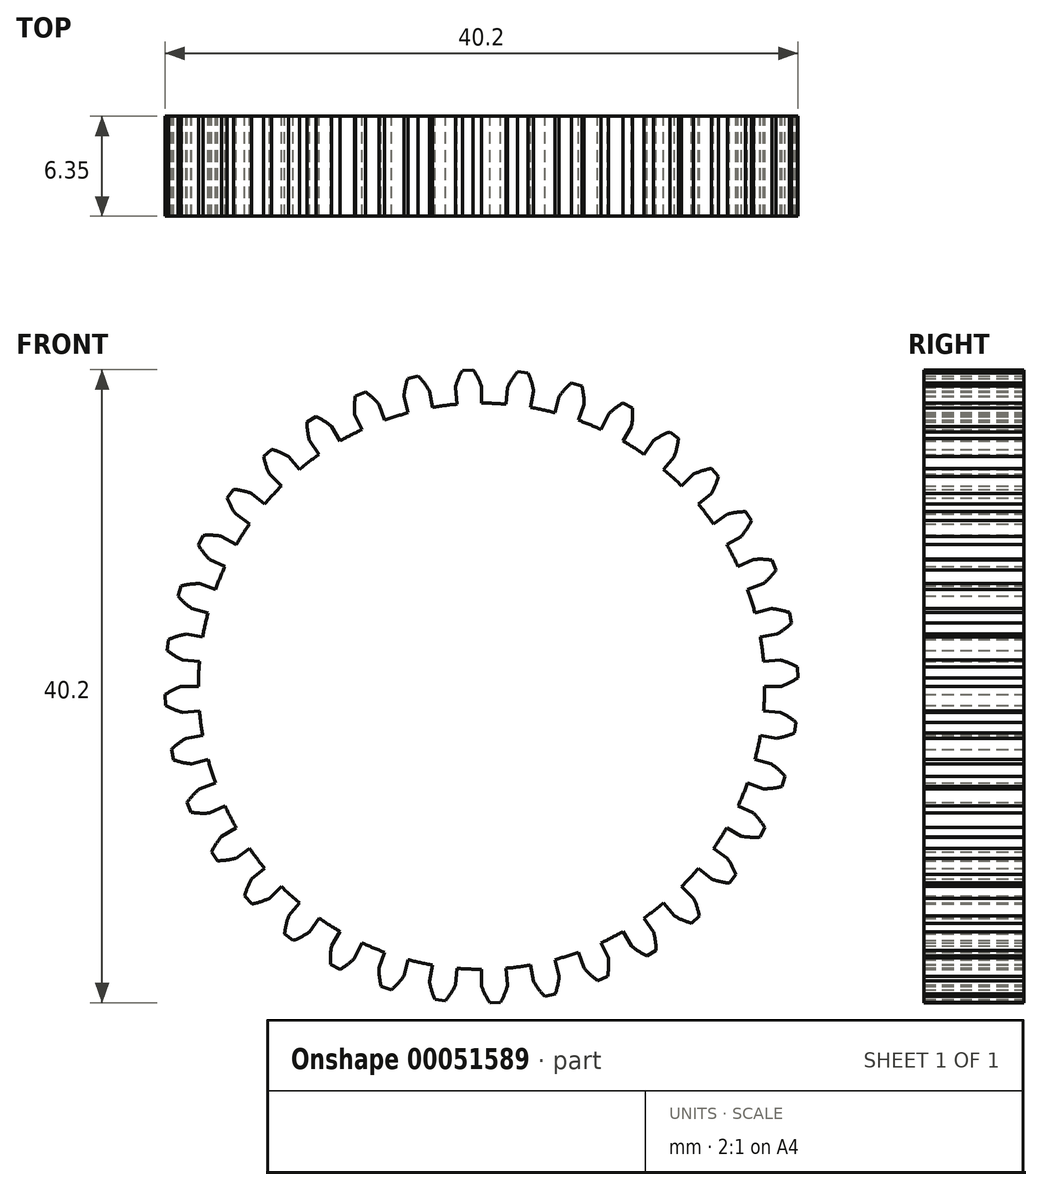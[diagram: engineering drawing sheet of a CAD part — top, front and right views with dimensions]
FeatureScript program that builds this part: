
annotation { "Feature Type Name" : "Feature", "Feature Type Description" : "" }
export const myFeature = defineFeature(function(context is Context, id is Id, definition is map)
    precondition{}
    {
        {
            var Q0;
            Q0=qCreatedBy(makeId("Front.planeOp"),FACE);
            var sketch = newSketch(context, id + "F0", { "sketchPlane" : qUnion([Q0])});
            skArc(sketch, "E0", {"start": v(-1.38, 17.93) * mm, "mid": v(-2.35, 17.83) * mm, "end": v(-3.3, 17.68) * mm});
            skArc(sketch, "E1.trimOffspring", {"start": v(0, 19.05) * mm, "mid": v(-0.24, 19.6) * mm, "end": v(-0.54, 20.1) * mm});
            skLineSegment(sketch, "E2", {"start": v(0, 19.05) * mm, "end": v(0, 17.98) * mm});
            skLineSegment(sketch, "E3", {"start": v(-0.54, 20.1) * mm, "end": v(-0.88, 20.08) * mm});
            skArc(sketch, "E4.MirrorCS", {"start": v(-1.66, 18.98) * mm, "mid": v(-1.47, 19.54) * mm, "end": v(-1.22, 20.07) * mm});
            skLineSegment(sketch, "E5.MirrorCS", {"start": v(-1.22, 20.07) * mm, "end": v(-0.88, 20.08) * mm});
            skLineSegment(sketch, "E6.MirrorCS", {"start": v(-1.66, 18.98) * mm, "end": v(-1.57, 17.91) * mm});
            skLineSegment(sketch, "E7.1.0", {"start": v(-4.93, 18.4) * mm, "end": v(-4.65, 17.37) * mm});
            skArc(sketch, "E7.1.1", {"start": v(-4.93, 18.4) * mm, "mid": v(-4.84, 18.98) * mm, "end": v(-4.68, 19.55) * mm});
            skLineSegment(sketch, "E7.1.2", {"start": v(-4.68, 19.55) * mm, "end": v(-4.35, 19.62) * mm});
            skLineSegment(sketch, "E7.1.3", {"start": v(-4.02, 19.7) * mm, "end": v(-4.35, 19.62) * mm});
            skArc(sketch, "E7.1.4", {"start": v(-3.3, 18.76) * mm, "mid": v(-3.63, 19.25) * mm, "end": v(-4.02, 19.7) * mm});
            skLineSegment(sketch, "E7.1.5", {"start": v(-3.3, 18.76) * mm, "end": v(-3.12, 17.7) * mm});
            skLineSegment(sketch, "E7.2.0", {"start": v(-8.05, 17.27) * mm, "end": v(-7.6, 16.3) * mm});
            skArc(sketch, "E7.2.1", {"start": v(-8.05, 17.27) * mm, "mid": v(-8.07, 17.85) * mm, "end": v(-8, 18.44) * mm});
            skLineSegment(sketch, "E7.2.2", {"start": v(-8, 18.44) * mm, "end": v(-7.7, 18.57) * mm});
            skLineSegment(sketch, "E7.2.3", {"start": v(-7.38, 18.7) * mm, "end": v(-7.7, 18.57) * mm});
            skArc(sketch, "E7.2.4", {"start": v(-6.52, 17.9) * mm, "mid": v(-6.92, 18.33) * mm, "end": v(-7.38, 18.7) * mm});
            skLineSegment(sketch, "E7.2.5", {"start": v(-6.52, 17.9) * mm, "end": v(-6.15, 16.9) * mm});
            skLineSegment(sketch, "E7.3.0", {"start": v(-10.93, 15.6) * mm, "end": v(-10.31, 14.73) * mm});
            skArc(sketch, "E7.3.1", {"start": v(-10.93, 15.6) * mm, "mid": v(-11.04, 16.18) * mm, "end": v(-11.09, 16.77) * mm});
            skLineSegment(sketch, "E7.3.2", {"start": v(-11.09, 16.77) * mm, "end": v(-10.8, 16.95) * mm});
            skLineSegment(sketch, "E7.3.3", {"start": v(-10.51, 17.14) * mm, "end": v(-10.8, 16.95) * mm});
            skArc(sketch, "E7.3.4", {"start": v(-9.52, 16.5) * mm, "mid": v(-10, 16.85) * mm, "end": v(-10.51, 17.14) * mm});
            skLineSegment(sketch, "E7.3.5", {"start": v(-9.52, 16.5) * mm, "end": v(-9, 15.57) * mm});
            skLineSegment(sketch, "E7.4.0", {"start": v(-13.47, 13.47) * mm, "end": v(-12.72, 12.72) * mm});
            skArc(sketch, "E7.4.1", {"start": v(-13.47, 13.47) * mm, "mid": v(-13.69, 14.02) * mm, "end": v(-13.83, 14.6) * mm});
            skLineSegment(sketch, "E7.4.2", {"start": v(-13.83, 14.6) * mm, "end": v(-13.58, 14.82) * mm});
            skLineSegment(sketch, "E7.4.3", {"start": v(-13.33, 15.05) * mm, "end": v(-13.58, 14.82) * mm});
            skArc(sketch, "E7.4.4", {"start": v(-12.25, 14.6) * mm, "mid": v(-12.77, 14.86) * mm, "end": v(-13.33, 15.05) * mm});
            skLineSegment(sketch, "E7.4.5", {"start": v(-12.25, 14.6) * mm, "end": v(-11.56, 13.78) * mm});
            skLineSegment(sketch, "E7.5.0", {"start": v(-15.6, 10.93) * mm, "end": v(-14.73, 10.31) * mm});
            skArc(sketch, "E7.5.1", {"start": v(-15.6, 10.93) * mm, "mid": v(-15.91, 11.43) * mm, "end": v(-16.15, 11.97) * mm});
            skLineSegment(sketch, "E7.5.2", {"start": v(-16.15, 11.97) * mm, "end": v(-15.95, 12.24) * mm});
            skLineSegment(sketch, "E7.5.3", {"start": v(-15.74, 12.5) * mm, "end": v(-15.95, 12.24) * mm});
            skArc(sketch, "E7.5.4", {"start": v(-14.6, 12.25) * mm, "mid": v(-15.16, 12.41) * mm, "end": v(-15.74, 12.5) * mm});
            skLineSegment(sketch, "E7.5.5", {"start": v(-14.6, 12.25) * mm, "end": v(-13.78, 11.56) * mm});
            skLineSegment(sketch, "E7.6.0", {"start": v(-17.27, 8.05) * mm, "end": v(-16.3, 7.6) * mm});
            skArc(sketch, "E7.6.1", {"start": v(-17.27, 8.05) * mm, "mid": v(-17.65, 8.5) * mm, "end": v(-17.99, 8.98) * mm});
            skLineSegment(sketch, "E7.6.2", {"start": v(-17.99, 8.98) * mm, "end": v(-17.83, 9.28) * mm});
            skLineSegment(sketch, "E7.6.3", {"start": v(-17.67, 9.58) * mm, "end": v(-17.83, 9.28) * mm});
            skArc(sketch, "E7.6.4", {"start": v(-16.5, 9.53) * mm, "mid": v(-17.08, 9.6) * mm, "end": v(-17.67, 9.58) * mm});
            skLineSegment(sketch, "E7.6.5", {"start": v(-16.5, 9.53) * mm, "end": v(-15.57, 9) * mm});
            skLineSegment(sketch, "E7.7.0", {"start": v(-18.4, 4.93) * mm, "end": v(-17.37, 4.65) * mm});
            skArc(sketch, "E7.7.1", {"start": v(-18.4, 4.93) * mm, "mid": v(-18.86, 5.3) * mm, "end": v(-19.27, 5.72) * mm});
            skLineSegment(sketch, "E7.7.2", {"start": v(-19.27, 5.72) * mm, "end": v(-19.17, 6.04) * mm});
            skLineSegment(sketch, "E7.7.3", {"start": v(-19.07, 6.37) * mm, "end": v(-19.17, 6.04) * mm});
            skArc(sketch, "E7.7.4", {"start": v(-17.9, 6.52) * mm, "mid": v(-18.49, 6.48) * mm, "end": v(-19.07, 6.37) * mm});
            skLineSegment(sketch, "E7.7.5", {"start": v(-17.9, 6.52) * mm, "end": v(-16.9, 6.15) * mm});
            skLineSegment(sketch, "E7.8.0", {"start": v(-18.98, 1.66) * mm, "end": v(-17.91, 1.57) * mm});
            skArc(sketch, "E7.8.1", {"start": v(-18.98, 1.66) * mm, "mid": v(-19.5, 1.94) * mm, "end": v(-19.97, 2.29) * mm});
            skLineSegment(sketch, "E7.8.2", {"start": v(-19.97, 2.29) * mm, "end": v(-19.93, 2.62) * mm});
            skLineSegment(sketch, "E7.8.3", {"start": v(-19.88, 2.96) * mm, "end": v(-19.93, 2.62) * mm});
            skArc(sketch, "E7.8.4", {"start": v(-18.76, 3.3) * mm, "mid": v(-19.33, 3.17) * mm, "end": v(-19.88, 2.96) * mm});
            skLineSegment(sketch, "E7.8.5", {"start": v(-18.76, 3.3) * mm, "end": v(-17.7, 3.12) * mm});
            skLineSegment(sketch, "E7.9.0", {"start": v(-18.98, -1.66) * mm, "end": v(-17.91, -1.57) * mm});
            skArc(sketch, "E7.9.1", {"start": v(-18.98, -1.66) * mm, "mid": v(-19.54, -1.47) * mm, "end": v(-20.07, -1.22) * mm});
            skLineSegment(sketch, "E7.9.2", {"start": v(-20.07, -1.22) * mm, "end": v(-20.08, -0.88) * mm});
            skLineSegment(sketch, "E7.9.3", {"start": v(-20.1, -0.54) * mm, "end": v(-20.08, -0.88) * mm});
            skArc(sketch, "E7.9.4", {"start": v(-19.05, 0) * mm, "mid": v(-19.6, -0.24) * mm, "end": v(-20.1, -0.54) * mm});
            skLineSegment(sketch, "E7.9.5", {"start": v(-19.05, 0) * mm, "end": v(-17.98, 0) * mm});
            skLineSegment(sketch, "E7.10.0", {"start": v(-18.4, -4.93) * mm, "end": v(-17.37, -4.65) * mm});
            skArc(sketch, "E7.10.1", {"start": v(-18.4, -4.93) * mm, "mid": v(-18.98, -4.84) * mm, "end": v(-19.55, -4.68) * mm});
            skLineSegment(sketch, "E7.10.2", {"start": v(-19.55, -4.68) * mm, "end": v(-19.62, -4.35) * mm});
            skLineSegment(sketch, "E7.10.3", {"start": v(-19.7, -4.02) * mm, "end": v(-19.62, -4.35) * mm});
            skArc(sketch, "E7.10.4", {"start": v(-18.76, -3.3) * mm, "mid": v(-19.25, -3.63) * mm, "end": v(-19.7, -4.02) * mm});
            skLineSegment(sketch, "E7.10.5", {"start": v(-18.76, -3.3) * mm, "end": v(-17.7, -3.12) * mm});
            skLineSegment(sketch, "E7.11.0", {"start": v(-17.27, -8.05) * mm, "end": v(-16.3, -7.6) * mm});
            skArc(sketch, "E7.11.1", {"start": v(-17.27, -8.05) * mm, "mid": v(-17.85, -8.07) * mm, "end": v(-18.44, -8) * mm});
            skLineSegment(sketch, "E7.11.2", {"start": v(-18.44, -8) * mm, "end": v(-18.57, -7.7) * mm});
            skLineSegment(sketch, "E7.11.3", {"start": v(-18.7, -7.38) * mm, "end": v(-18.57, -7.7) * mm});
            skArc(sketch, "E7.11.4", {"start": v(-17.9, -6.52) * mm, "mid": v(-18.33, -6.92) * mm, "end": v(-18.7, -7.38) * mm});
            skLineSegment(sketch, "E7.11.5", {"start": v(-17.9, -6.52) * mm, "end": v(-16.9, -6.15) * mm});
            skLineSegment(sketch, "E7.12.0", {"start": v(-15.6, -10.93) * mm, "end": v(-14.73, -10.31) * mm});
            skArc(sketch, "E7.12.1", {"start": v(-15.6, -10.93) * mm, "mid": v(-16.18, -11.04) * mm, "end": v(-16.77, -11.09) * mm});
            skLineSegment(sketch, "E7.12.2", {"start": v(-16.77, -11.09) * mm, "end": v(-16.95, -10.8) * mm});
            skLineSegment(sketch, "E7.12.3", {"start": v(-17.14, -10.51) * mm, "end": v(-16.95, -10.8) * mm});
            skArc(sketch, "E7.12.4", {"start": v(-16.5, -9.52) * mm, "mid": v(-16.85, -10) * mm, "end": v(-17.14, -10.51) * mm});
            skLineSegment(sketch, "E7.12.5", {"start": v(-16.5, -9.52) * mm, "end": v(-15.57, -9) * mm});
            skLineSegment(sketch, "E7.13.0", {"start": v(-13.47, -13.47) * mm, "end": v(-12.72, -12.72) * mm});
            skArc(sketch, "E7.13.1", {"start": v(-13.47, -13.47) * mm, "mid": v(-14.02, -13.69) * mm, "end": v(-14.6, -13.83) * mm});
            skLineSegment(sketch, "E7.13.2", {"start": v(-14.6, -13.83) * mm, "end": v(-14.82, -13.58) * mm});
            skLineSegment(sketch, "E7.13.3", {"start": v(-15.05, -13.33) * mm, "end": v(-14.82, -13.58) * mm});
            skArc(sketch, "E7.13.4", {"start": v(-14.6, -12.25) * mm, "mid": v(-14.86, -12.77) * mm, "end": v(-15.05, -13.33) * mm});
            skLineSegment(sketch, "E7.13.5", {"start": v(-14.6, -12.25) * mm, "end": v(-13.78, -11.56) * mm});
            skLineSegment(sketch, "E7.14.0", {"start": v(-10.93, -15.6) * mm, "end": v(-10.31, -14.73) * mm});
            skArc(sketch, "E7.14.1", {"start": v(-10.93, -15.6) * mm, "mid": v(-11.43, -15.91) * mm, "end": v(-11.97, -16.15) * mm});
            skLineSegment(sketch, "E7.14.2", {"start": v(-11.97, -16.15) * mm, "end": v(-12.24, -15.95) * mm});
            skLineSegment(sketch, "E7.14.3", {"start": v(-12.5, -15.74) * mm, "end": v(-12.24, -15.95) * mm});
            skArc(sketch, "E7.14.4", {"start": v(-12.25, -14.6) * mm, "mid": v(-12.41, -15.16) * mm, "end": v(-12.5, -15.74) * mm});
            skLineSegment(sketch, "E7.14.5", {"start": v(-12.25, -14.6) * mm, "end": v(-11.56, -13.78) * mm});
            skLineSegment(sketch, "E7.15.0", {"start": v(-8.05, -17.27) * mm, "end": v(-7.6, -16.3) * mm});
            skArc(sketch, "E7.15.1", {"start": v(-8.05, -17.27) * mm, "mid": v(-8.5, -17.65) * mm, "end": v(-8.98, -17.99) * mm});
            skLineSegment(sketch, "E7.15.2", {"start": v(-8.98, -17.99) * mm, "end": v(-9.28, -17.83) * mm});
            skLineSegment(sketch, "E7.15.3", {"start": v(-9.58, -17.67) * mm, "end": v(-9.28, -17.83) * mm});
            skArc(sketch, "E7.15.4", {"start": v(-9.53, -16.5) * mm, "mid": v(-9.6, -17.08) * mm, "end": v(-9.58, -17.67) * mm});
            skLineSegment(sketch, "E7.15.5", {"start": v(-9.53, -16.5) * mm, "end": v(-9, -15.57) * mm});
            skLineSegment(sketch, "E7.16.0", {"start": v(-4.93, -18.4) * mm, "end": v(-4.65, -17.37) * mm});
            skArc(sketch, "E7.16.1", {"start": v(-4.93, -18.4) * mm, "mid": v(-5.3, -18.86) * mm, "end": v(-5.72, -19.27) * mm});
            skLineSegment(sketch, "E7.16.2", {"start": v(-5.72, -19.27) * mm, "end": v(-6.04, -19.17) * mm});
            skLineSegment(sketch, "E7.16.3", {"start": v(-6.37, -19.07) * mm, "end": v(-6.04, -19.17) * mm});
            skArc(sketch, "E7.16.4", {"start": v(-6.52, -17.9) * mm, "mid": v(-6.48, -18.49) * mm, "end": v(-6.37, -19.07) * mm});
            skLineSegment(sketch, "E7.16.5", {"start": v(-6.52, -17.9) * mm, "end": v(-6.15, -16.9) * mm});
            skLineSegment(sketch, "E7.17.0", {"start": v(-1.66, -18.98) * mm, "end": v(-1.57, -17.91) * mm});
            skArc(sketch, "E7.17.1", {"start": v(-1.66, -18.98) * mm, "mid": v(-1.94, -19.5) * mm, "end": v(-2.29, -19.97) * mm});
            skLineSegment(sketch, "E7.17.2", {"start": v(-2.29, -19.97) * mm, "end": v(-2.62, -19.93) * mm});
            skLineSegment(sketch, "E7.17.3", {"start": v(-2.96, -19.88) * mm, "end": v(-2.62, -19.93) * mm});
            skArc(sketch, "E7.17.4", {"start": v(-3.3, -18.76) * mm, "mid": v(-3.17, -19.33) * mm, "end": v(-2.96, -19.88) * mm});
            skLineSegment(sketch, "E7.17.5", {"start": v(-3.3, -18.76) * mm, "end": v(-3.12, -17.7) * mm});
            skLineSegment(sketch, "E7.18.0", {"start": v(1.66, -18.98) * mm, "end": v(1.57, -17.91) * mm});
            skArc(sketch, "E7.18.1", {"start": v(1.66, -18.98) * mm, "mid": v(1.47, -19.54) * mm, "end": v(1.22, -20.07) * mm});
            skLineSegment(sketch, "E7.18.2", {"start": v(1.22, -20.07) * mm, "end": v(0.88, -20.08) * mm});
            skLineSegment(sketch, "E7.18.3", {"start": v(0.54, -20.1) * mm, "end": v(0.88, -20.08) * mm});
            skArc(sketch, "E7.18.4", {"start": v(0, -19.05) * mm, "mid": v(0.24, -19.6) * mm, "end": v(0.54, -20.1) * mm});
            skLineSegment(sketch, "E7.18.5", {"start": v(0, -19.05) * mm, "end": v(0, -17.98) * mm});
            skLineSegment(sketch, "E7.19.0", {"start": v(4.93, -18.4) * mm, "end": v(4.65, -17.37) * mm});
            skArc(sketch, "E7.19.1", {"start": v(4.93, -18.4) * mm, "mid": v(4.84, -18.98) * mm, "end": v(4.68, -19.55) * mm});
            skLineSegment(sketch, "E7.19.2", {"start": v(4.68, -19.55) * mm, "end": v(4.35, -19.62) * mm});
            skLineSegment(sketch, "E7.19.3", {"start": v(4.02, -19.7) * mm, "end": v(4.35, -19.62) * mm});
            skArc(sketch, "E7.19.4", {"start": v(3.3, -18.76) * mm, "mid": v(3.63, -19.25) * mm, "end": v(4.02, -19.7) * mm});
            skLineSegment(sketch, "E7.19.5", {"start": v(3.3, -18.76) * mm, "end": v(3.12, -17.7) * mm});
            skLineSegment(sketch, "E7.20.0", {"start": v(8.05, -17.27) * mm, "end": v(7.6, -16.3) * mm});
            skArc(sketch, "E7.20.1", {"start": v(8.05, -17.27) * mm, "mid": v(8.07, -17.85) * mm, "end": v(8, -18.44) * mm});
            skLineSegment(sketch, "E7.20.2", {"start": v(8, -18.44) * mm, "end": v(7.7, -18.57) * mm});
            skLineSegment(sketch, "E7.20.3", {"start": v(7.38, -18.7) * mm, "end": v(7.7, -18.57) * mm});
            skArc(sketch, "E7.20.4", {"start": v(6.52, -17.9) * mm, "mid": v(6.92, -18.33) * mm, "end": v(7.38, -18.7) * mm});
            skLineSegment(sketch, "E7.20.5", {"start": v(6.52, -17.9) * mm, "end": v(6.15, -16.9) * mm});
            skLineSegment(sketch, "E7.21.0", {"start": v(10.93, -15.6) * mm, "end": v(10.31, -14.73) * mm});
            skArc(sketch, "E7.21.1", {"start": v(10.93, -15.6) * mm, "mid": v(11.04, -16.18) * mm, "end": v(11.09, -16.77) * mm});
            skLineSegment(sketch, "E7.21.2", {"start": v(11.09, -16.77) * mm, "end": v(10.8, -16.95) * mm});
            skLineSegment(sketch, "E7.21.3", {"start": v(10.51, -17.14) * mm, "end": v(10.8, -16.95) * mm});
            skArc(sketch, "E7.21.4", {"start": v(9.53, -16.5) * mm, "mid": v(10, -16.85) * mm, "end": v(10.51, -17.14) * mm});
            skLineSegment(sketch, "E7.21.5", {"start": v(9.53, -16.5) * mm, "end": v(9, -15.57) * mm});
            skLineSegment(sketch, "E7.22.0", {"start": v(13.47, -13.47) * mm, "end": v(12.72, -12.72) * mm});
            skArc(sketch, "E7.22.1", {"start": v(13.47, -13.47) * mm, "mid": v(13.69, -14.02) * mm, "end": v(13.83, -14.6) * mm});
            skLineSegment(sketch, "E7.22.2", {"start": v(13.83, -14.6) * mm, "end": v(13.58, -14.82) * mm});
            skLineSegment(sketch, "E7.22.3", {"start": v(13.33, -15.05) * mm, "end": v(13.58, -14.82) * mm});
            skArc(sketch, "E7.22.4", {"start": v(12.25, -14.6) * mm, "mid": v(12.77, -14.86) * mm, "end": v(13.33, -15.05) * mm});
            skLineSegment(sketch, "E7.22.5", {"start": v(12.25, -14.6) * mm, "end": v(11.56, -13.78) * mm});
            skLineSegment(sketch, "E7.23.0", {"start": v(15.6, -10.93) * mm, "end": v(14.73, -10.31) * mm});
            skArc(sketch, "E7.23.1", {"start": v(15.6, -10.93) * mm, "mid": v(15.91, -11.43) * mm, "end": v(16.15, -11.97) * mm});
            skLineSegment(sketch, "E7.23.2", {"start": v(16.15, -11.97) * mm, "end": v(15.95, -12.24) * mm});
            skLineSegment(sketch, "E7.23.3", {"start": v(15.74, -12.5) * mm, "end": v(15.95, -12.24) * mm});
            skArc(sketch, "E7.23.4", {"start": v(14.6, -12.25) * mm, "mid": v(15.16, -12.41) * mm, "end": v(15.74, -12.5) * mm});
            skLineSegment(sketch, "E7.23.5", {"start": v(14.6, -12.25) * mm, "end": v(13.78, -11.56) * mm});
            skLineSegment(sketch, "E7.24.0", {"start": v(17.27, -8.05) * mm, "end": v(16.3, -7.6) * mm});
            skArc(sketch, "E7.24.1", {"start": v(17.27, -8.05) * mm, "mid": v(17.65, -8.5) * mm, "end": v(17.99, -8.98) * mm});
            skLineSegment(sketch, "E7.24.2", {"start": v(17.99, -8.98) * mm, "end": v(17.83, -9.28) * mm});
            skLineSegment(sketch, "E7.24.3", {"start": v(17.67, -9.58) * mm, "end": v(17.83, -9.28) * mm});
            skArc(sketch, "E7.24.4", {"start": v(16.5, -9.53) * mm, "mid": v(17.08, -9.6) * mm, "end": v(17.67, -9.58) * mm});
            skLineSegment(sketch, "E7.24.5", {"start": v(16.5, -9.53) * mm, "end": v(15.57, -9) * mm});
            skLineSegment(sketch, "E7.25.0", {"start": v(18.4, -4.93) * mm, "end": v(17.37, -4.65) * mm});
            skArc(sketch, "E7.25.1", {"start": v(18.4, -4.93) * mm, "mid": v(18.86, -5.3) * mm, "end": v(19.27, -5.72) * mm});
            skLineSegment(sketch, "E7.25.2", {"start": v(19.27, -5.72) * mm, "end": v(19.17, -6.04) * mm});
            skLineSegment(sketch, "E7.25.3", {"start": v(19.07, -6.37) * mm, "end": v(19.17, -6.04) * mm});
            skArc(sketch, "E7.25.4", {"start": v(17.9, -6.52) * mm, "mid": v(18.49, -6.48) * mm, "end": v(19.07, -6.37) * mm});
            skLineSegment(sketch, "E7.25.5", {"start": v(17.9, -6.52) * mm, "end": v(16.9, -6.15) * mm});
            skLineSegment(sketch, "E7.26.0", {"start": v(18.98, -1.66) * mm, "end": v(17.91, -1.57) * mm});
            skArc(sketch, "E7.26.1", {"start": v(18.98, -1.66) * mm, "mid": v(19.5, -1.94) * mm, "end": v(19.97, -2.29) * mm});
            skLineSegment(sketch, "E7.26.2", {"start": v(19.97, -2.29) * mm, "end": v(19.93, -2.62) * mm});
            skLineSegment(sketch, "E7.26.3", {"start": v(19.88, -2.96) * mm, "end": v(19.93, -2.62) * mm});
            skArc(sketch, "E7.26.4", {"start": v(18.76, -3.3) * mm, "mid": v(19.33, -3.17) * mm, "end": v(19.88, -2.96) * mm});
            skLineSegment(sketch, "E7.26.5", {"start": v(18.76, -3.3) * mm, "end": v(17.7, -3.12) * mm});
            skLineSegment(sketch, "E7.27.0", {"start": v(18.98, 1.66) * mm, "end": v(17.91, 1.57) * mm});
            skArc(sketch, "E7.27.1", {"start": v(18.98, 1.66) * mm, "mid": v(19.54, 1.47) * mm, "end": v(20.07, 1.22) * mm});
            skLineSegment(sketch, "E7.27.2", {"start": v(20.07, 1.22) * mm, "end": v(20.08, 0.88) * mm});
            skLineSegment(sketch, "E7.27.3", {"start": v(20.1, 0.54) * mm, "end": v(20.08, 0.88) * mm});
            skArc(sketch, "E7.27.4", {"start": v(19.05, 0) * mm, "mid": v(19.6, 0.24) * mm, "end": v(20.1, 0.54) * mm});
            skLineSegment(sketch, "E7.27.5", {"start": v(19.05, 0) * mm, "end": v(17.98, 0) * mm});
            skLineSegment(sketch, "E7.28.0", {"start": v(18.4, 4.93) * mm, "end": v(17.37, 4.65) * mm});
            skArc(sketch, "E7.28.1", {"start": v(18.4, 4.93) * mm, "mid": v(18.98, 4.84) * mm, "end": v(19.55, 4.68) * mm});
            skLineSegment(sketch, "E7.28.2", {"start": v(19.55, 4.68) * mm, "end": v(19.62, 4.35) * mm});
            skLineSegment(sketch, "E7.28.3", {"start": v(19.7, 4.02) * mm, "end": v(19.62, 4.35) * mm});
            skArc(sketch, "E7.28.4", {"start": v(18.76, 3.3) * mm, "mid": v(19.25, 3.63) * mm, "end": v(19.7, 4.02) * mm});
            skLineSegment(sketch, "E7.28.5", {"start": v(18.76, 3.3) * mm, "end": v(17.7, 3.12) * mm});
            skLineSegment(sketch, "E7.29.0", {"start": v(17.27, 8.05) * mm, "end": v(16.3, 7.6) * mm});
            skArc(sketch, "E7.29.1", {"start": v(17.27, 8.05) * mm, "mid": v(17.85, 8.07) * mm, "end": v(18.44, 8) * mm});
            skLineSegment(sketch, "E7.29.2", {"start": v(18.44, 8) * mm, "end": v(18.57, 7.7) * mm});
            skLineSegment(sketch, "E7.29.3", {"start": v(18.7, 7.38) * mm, "end": v(18.57, 7.7) * mm});
            skArc(sketch, "E7.29.4", {"start": v(17.9, 6.52) * mm, "mid": v(18.33, 6.92) * mm, "end": v(18.7, 7.38) * mm});
            skLineSegment(sketch, "E7.29.5", {"start": v(17.9, 6.52) * mm, "end": v(16.9, 6.15) * mm});
            skLineSegment(sketch, "E7.30.0", {"start": v(15.6, 10.93) * mm, "end": v(14.73, 10.31) * mm});
            skArc(sketch, "E7.30.1", {"start": v(15.6, 10.93) * mm, "mid": v(16.18, 11.04) * mm, "end": v(16.77, 11.09) * mm});
            skLineSegment(sketch, "E7.30.2", {"start": v(16.77, 11.09) * mm, "end": v(16.95, 10.8) * mm});
            skLineSegment(sketch, "E7.30.3", {"start": v(17.14, 10.51) * mm, "end": v(16.95, 10.8) * mm});
            skArc(sketch, "E7.30.4", {"start": v(16.5, 9.52) * mm, "mid": v(16.85, 10) * mm, "end": v(17.14, 10.51) * mm});
            skLineSegment(sketch, "E7.30.5", {"start": v(16.5, 9.52) * mm, "end": v(15.57, 9) * mm});
            skLineSegment(sketch, "E7.31.0", {"start": v(13.47, 13.47) * mm, "end": v(12.72, 12.72) * mm});
            skArc(sketch, "E7.31.1", {"start": v(13.47, 13.47) * mm, "mid": v(14.02, 13.69) * mm, "end": v(14.6, 13.83) * mm});
            skLineSegment(sketch, "E7.31.2", {"start": v(14.6, 13.83) * mm, "end": v(14.82, 13.58) * mm});
            skLineSegment(sketch, "E7.31.3", {"start": v(15.05, 13.33) * mm, "end": v(14.82, 13.58) * mm});
            skArc(sketch, "E7.31.4", {"start": v(14.6, 12.25) * mm, "mid": v(14.86, 12.77) * mm, "end": v(15.05, 13.33) * mm});
            skLineSegment(sketch, "E7.31.5", {"start": v(14.6, 12.25) * mm, "end": v(13.78, 11.56) * mm});
            skLineSegment(sketch, "E7.32.0", {"start": v(10.93, 15.6) * mm, "end": v(10.31, 14.73) * mm});
            skArc(sketch, "E7.32.1", {"start": v(10.93, 15.6) * mm, "mid": v(11.43, 15.91) * mm, "end": v(11.97, 16.15) * mm});
            skLineSegment(sketch, "E7.32.2", {"start": v(11.97, 16.15) * mm, "end": v(12.24, 15.95) * mm});
            skLineSegment(sketch, "E7.32.3", {"start": v(12.5, 15.74) * mm, "end": v(12.24, 15.95) * mm});
            skArc(sketch, "E7.32.4", {"start": v(12.25, 14.6) * mm, "mid": v(12.41, 15.16) * mm, "end": v(12.5, 15.74) * mm});
            skLineSegment(sketch, "E7.32.5", {"start": v(12.25, 14.6) * mm, "end": v(11.56, 13.78) * mm});
            skLineSegment(sketch, "E7.33.0", {"start": v(8.05, 17.27) * mm, "end": v(7.6, 16.3) * mm});
            skArc(sketch, "E7.33.1", {"start": v(8.05, 17.27) * mm, "mid": v(8.5, 17.65) * mm, "end": v(8.98, 17.99) * mm});
            skLineSegment(sketch, "E7.33.2", {"start": v(8.98, 17.99) * mm, "end": v(9.28, 17.83) * mm});
            skLineSegment(sketch, "E7.33.3", {"start": v(9.58, 17.67) * mm, "end": v(9.28, 17.83) * mm});
            skArc(sketch, "E7.33.4", {"start": v(9.52, 16.5) * mm, "mid": v(9.6, 17.08) * mm, "end": v(9.58, 17.67) * mm});
            skLineSegment(sketch, "E7.33.5", {"start": v(9.52, 16.5) * mm, "end": v(9, 15.57) * mm});
            skLineSegment(sketch, "E7.34.0", {"start": v(4.93, 18.4) * mm, "end": v(4.65, 17.37) * mm});
            skArc(sketch, "E7.34.1", {"start": v(4.93, 18.4) * mm, "mid": v(5.3, 18.86) * mm, "end": v(5.72, 19.27) * mm});
            skLineSegment(sketch, "E7.34.2", {"start": v(5.72, 19.27) * mm, "end": v(6.04, 19.17) * mm});
            skLineSegment(sketch, "E7.34.3", {"start": v(6.37, 19.07) * mm, "end": v(6.04, 19.17) * mm});
            skArc(sketch, "E7.34.4", {"start": v(6.52, 17.9) * mm, "mid": v(6.48, 18.49) * mm, "end": v(6.37, 19.07) * mm});
            skLineSegment(sketch, "E7.34.5", {"start": v(6.52, 17.9) * mm, "end": v(6.15, 16.9) * mm});
            skLineSegment(sketch, "E7.35.0", {"start": v(1.66, 18.98) * mm, "end": v(1.57, 17.91) * mm});
            skArc(sketch, "E7.35.1", {"start": v(1.66, 18.98) * mm, "mid": v(1.94, 19.5) * mm, "end": v(2.29, 19.97) * mm});
            skLineSegment(sketch, "E7.35.2", {"start": v(2.29, 19.97) * mm, "end": v(2.62, 19.93) * mm});
            skLineSegment(sketch, "E7.35.3", {"start": v(2.96, 19.88) * mm, "end": v(2.62, 19.93) * mm});
            skArc(sketch, "E7.35.4", {"start": v(3.3, 18.76) * mm, "mid": v(3.17, 19.33) * mm, "end": v(2.96, 19.88) * mm});
            skLineSegment(sketch, "E7.35.5", {"start": v(3.3, 18.76) * mm, "end": v(3.12, 17.7) * mm});
            skArc(sketch, "E8.trimOffspring", {"start": v(1.75, 17.9) * mm, "mid": v(0.78, 17.97) * mm, "end": v(-0.19, 17.98) * mm});
            skArc(sketch, "E9.trimOffspring", {"start": v(4.83, 17.32) * mm, "mid": v(3.9, 17.56) * mm, "end": v(2.94, 17.74) * mm});
            skArc(sketch, "E10.trimOffspring", {"start": v(7.77, 16.22) * mm, "mid": v(6.88, 16.61) * mm, "end": v(5.98, 16.96) * mm});
            skArc(sketch, "E11.trimOffspring", {"start": v(10.47, 14.62) * mm, "mid": v(9.66, 15.17) * mm, "end": v(8.83, 15.67) * mm});
            skArc(sketch, "E12.trimOffspring", {"start": v(12.85, 12.58) * mm, "mid": v(12.15, 13.26) * mm, "end": v(11.42, 13.9) * mm});
            skArc(sketch, "E13.trimOffspring", {"start": v(14.84, 10.16) * mm, "mid": v(14.27, 10.95) * mm, "end": v(13.66, 11.7) * mm});
            skArc(sketch, "E14.trimOffspring", {"start": v(16.38, 7.43) * mm, "mid": v(15.95, 8.3) * mm, "end": v(15.48, 9.15) * mm});
            skArc(sketch, "E15.trimOffspring", {"start": v(17.42, 4.47) * mm, "mid": v(17.18, 5.32) * mm, "end": v(16.9, 6.15) * mm});
            skArc(sketch, "E16.trimOffspring", {"start": v(17.93, 1.38) * mm, "mid": v(17.83, 2.35) * mm, "end": v(17.68, 3.3) * mm});
            skArc(sketch, "E17.trimOffspring", {"start": v(17.9, -1.75) * mm, "mid": v(17.97, -0.78) * mm, "end": v(17.98, 0.19) * mm});
            skArc(sketch, "E18.trimOffspring", {"start": v(17.32, -4.83) * mm, "mid": v(17.56, -3.9) * mm, "end": v(17.74, -2.94) * mm});
            skArc(sketch, "E19.trimOffspring", {"start": v(16.22, -7.77) * mm, "mid": v(16.61, -6.88) * mm, "end": v(16.96, -5.98) * mm});
            skArc(sketch, "E20.trimOffspring", {"start": v(14.62, -10.47) * mm, "mid": v(15.17, -9.66) * mm, "end": v(15.67, -8.83) * mm});
            skArc(sketch, "E21.trimOffspring", {"start": v(12.58, -12.85) * mm, "mid": v(13.26, -12.15) * mm, "end": v(13.9, -11.42) * mm});
            skArc(sketch, "E22.trimOffspring", {"start": v(10.16, -14.84) * mm, "mid": v(10.95, -14.27) * mm, "end": v(11.7, -13.66) * mm});
            skArc(sketch, "E23.trimOffspring", {"start": v(7.43, -16.38) * mm, "mid": v(8.3, -15.95) * mm, "end": v(9.15, -15.48) * mm});
            skArc(sketch, "E24.trimOffspring", {"start": v(4.47, -17.42) * mm, "mid": v(5.4, -17.15) * mm, "end": v(6.33, -16.83) * mm});
            skArc(sketch, "E25.trimOffspring", {"start": v(1.38, -17.93) * mm, "mid": v(2.35, -17.83) * mm, "end": v(3.3, -17.68) * mm});
            skArc(sketch, "E26.trimOffspring", {"start": v(-1.75, -17.9) * mm, "mid": v(-0.78, -17.97) * mm, "end": v(0.19, -17.98) * mm});
            skArc(sketch, "E27.trimOffspring", {"start": v(-4.83, -17.32) * mm, "mid": v(-3.9, -17.56) * mm, "end": v(-2.94, -17.74) * mm});
            skArc(sketch, "E28.trimOffspring", {"start": v(-7.77, -16.22) * mm, "mid": v(-6.88, -16.61) * mm, "end": v(-5.98, -16.96) * mm});
            skArc(sketch, "E29.trimOffspring", {"start": v(-10.47, -14.62) * mm, "mid": v(-9.66, -15.17) * mm, "end": v(-8.83, -15.67) * mm});
            skArc(sketch, "E30.trimOffspring", {"start": v(-12.85, -12.58) * mm, "mid": v(-12.15, -13.26) * mm, "end": v(-11.42, -13.9) * mm});
            skArc(sketch, "E31.trimOffspring", {"start": v(-14.84, -10.16) * mm, "mid": v(-14.27, -10.95) * mm, "end": v(-13.66, -11.7) * mm});
            skArc(sketch, "E32.trimOffspring", {"start": v(-16.38, -7.43) * mm, "mid": v(-15.95, -8.3) * mm, "end": v(-15.48, -9.15) * mm});
            skArc(sketch, "E33.trimOffspring", {"start": v(-17.42, -4.47) * mm, "mid": v(-17.15, -5.4) * mm, "end": v(-16.83, -6.33) * mm});
            skArc(sketch, "E34.trimOffspring", {"start": v(-17.93, -1.38) * mm, "mid": v(-17.84, -2.25) * mm, "end": v(-17.7, -3.12) * mm});
            skArc(sketch, "E35.trimOffspring", {"start": v(-17.9, 1.75) * mm, "mid": v(-17.97, 0.78) * mm, "end": v(-17.98, -0.19) * mm});
            skArc(sketch, "E36.trimOffspring", {"start": v(-17.32, 4.83) * mm, "mid": v(-17.56, 3.9) * mm, "end": v(-17.74, 2.94) * mm});
            skArc(sketch, "E37.trimOffspring", {"start": v(-16.22, 7.77) * mm, "mid": v(-16.58, 6.97) * mm, "end": v(-16.9, 6.15) * mm});
            skArc(sketch, "E38.trimOffspring", {"start": v(-14.62, 10.47) * mm, "mid": v(-15.17, 9.66) * mm, "end": v(-15.67, 8.83) * mm});
            skArc(sketch, "E39.trimOffspring", {"start": v(-12.58, 12.85) * mm, "mid": v(-13.26, 12.15) * mm, "end": v(-13.9, 11.42) * mm});
            skArc(sketch, "E40.trimOffspring", {"start": v(-10.16, 14.84) * mm, "mid": v(-10.95, 14.27) * mm, "end": v(-11.7, 13.66) * mm});
            skArc(sketch, "E41.trimOffspring", {"start": v(-7.43, 16.38) * mm, "mid": v(-8.3, 15.95) * mm, "end": v(-9.15, 15.48) * mm});
            skArc(sketch, "E42.trimOffspring", {"start": v(-4.47, 17.42) * mm, "mid": v(-5.4, 17.15) * mm, "end": v(-6.33, 16.83) * mm});
            skSolve(sketch);
        }
        {
            var Q0;
            Q0 = qSketchRegion(id + "F0", true);
            extrude(context, id + "F1", {"entities" : qUnion([Q0]), "depth" : 6.35 * mm});
        }
    });
